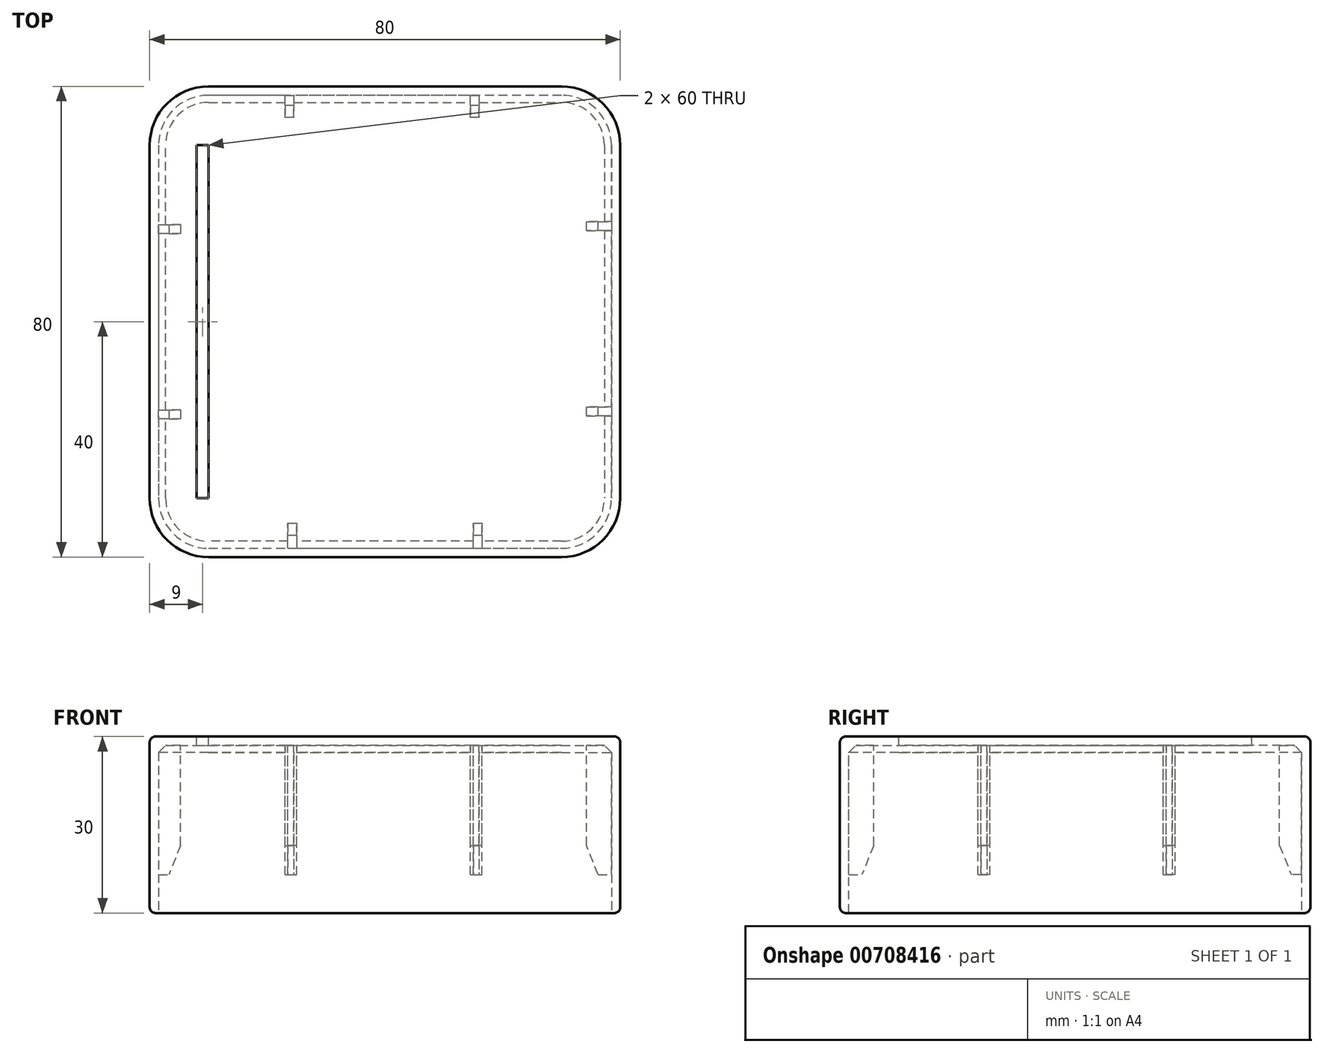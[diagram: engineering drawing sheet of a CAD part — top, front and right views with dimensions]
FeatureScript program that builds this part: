
annotation { "Feature Type Name" : "Feature", "Feature Type Description" : "" }
export const myFeature = defineFeature(function(context is Context, id is Id, definition is map)
    precondition{}
    {
        {
            var Q0;
            Q0=qCreatedBy(makeId("Top.planeOp"),FACE);
            var sketch = newSketch(context, id + "F0", { "sketchPlane" : qUnion([Q0])});
            skLineSegment(sketch, "E0", {"start": v(10, 20) * mm, "end": v(-50, 20) * mm});
            skLineSegment(sketch, "E1", {"start": v(-60, 10) * mm, "end": v(-60, -50) * mm});
            skPoint(sketch, "E2.visualSharp", {"position": v(-60, -60) * mm});
            skPoint(sketch, "E3.visualSharp", {"position": v(20, 20) * mm});
            skArc(sketch, "E3.filletArc", {"start": v(20, 10) * mm, "mid": v(17.07, 17.07) * mm, "end": v(10, 20) * mm});
            skPoint(sketch, "E4.visualSharp", {"position": v(-60, 20) * mm});
            skArc(sketch, "E4.filletArc", {"start": v(-50, 20) * mm, "mid": v(-57.07, 17.07) * mm, "end": v(-60, 10) * mm});
            skPoint(sketch, "E5.visualSharp", {"position": v(20, -60) * mm});
            skArc(sketch, "E6.filletArc", {"start": v(-60, -50) * mm, "mid": v(-57.07, -57.07) * mm, "end": v(-50, -60) * mm});
            skLineSegment(sketch, "E7", {"start": v(-50, -60) * mm, "end": v(10, -60) * mm});
            skLineSegment(sketch, "E8", {"start": v(20, 10) * mm, "end": v(20, -50) * mm});
            skArc(sketch, "E9.filletArc", {"start": v(10, -60) * mm, "mid": v(17.07, -57.07) * mm, "end": v(20, -50) * mm});
            skLineSegment(sketch, "E10", {"start": v(20, 20) * mm, "end": v(10, 20) * mm, "construction": true});
            skLineSegment(sketch, "E11", {"start": v(20, 20) * mm, "end": v(20, 10) * mm, "construction": true});
            skLineSegment(sketch, "E12", {"start": v(-50, 20) * mm, "end": v(-60, 20) * mm, "construction": true});
            skLineSegment(sketch, "E13", {"start": v(-60, 20) * mm, "end": v(-60, 10) * mm, "construction": true});
            skLineSegment(sketch, "E14", {"start": v(-60, -50) * mm, "end": v(-60, -60) * mm, "construction": true});
            skLineSegment(sketch, "E15", {"start": v(-60, -60) * mm, "end": v(-50, -60) * mm, "construction": true});
            skLineSegment(sketch, "E16", {"start": v(20, -50) * mm, "end": v(20, -60) * mm, "construction": true});
            skLineSegment(sketch, "E17", {"start": v(20, -60) * mm, "end": v(10, -60) * mm, "construction": true});
            skSolve(sketch);
        }
        {
            var Q0;
            Q0=makeQuery(id+"F0.imprint","IMPRINT",FACE,{"disambiguationData":[TD([[makeQuery(id+"F0.imprint","IMPRINT",EDGE,{"derivedFrom":sQuery(id+"F0.wireOp",EDGE,"E0")}),1.0]])]});
            extrude(context, id + "F1", {"entities" : qUnion([Q0]), "depth" : 30 * mm});
        }
        {
            var Q0;
            Q0=makeQuery(id+"F1.opExtrude","CAP_FACE",FACE,{"disambiguationData":[OSD([sQuery(id+"F0.wireOp",EDGE,"E0"),sQuery(id+"F0.wireOp",EDGE,"E1"),sQuery(id+"F0.wireOp",EDGE,"tLIrDgZX-HZ4B-HLsu-Evyy-lOQtlpBdo2Ac"),sQuery(id+"F0.wireOp",EDGE,"E3.filletArc"),sQuery(id+"F0.wireOp",EDGE,"E4.filletArc"),sQuery(id+"F0.wireOp",EDGE,"E5.filletArc"),sQuery(id+"F0.wireOp",EDGE,"yPNshCSU-yKMU-eblL-DxmT-mCKaPt0DpMVh"),sQuery(id+"F0.wireOp",EDGE,"E6.filletArc")])],"isStart":true});
            shell(context, id + "F2", {"entities" : qUnion([Q0]), "thickness" : 1.5 * mm});
        }
        {
            var Q0;
            Q0=makeQuery(id+"F2.opShell","OFFSET_FACE",FACE,{"disambiguationData":[OSD([sQuery(id+"F0.wireOp",EDGE,"E0"),sQuery(id+"F0.wireOp",EDGE,"E1"),sQuery(id+"F0.wireOp",EDGE,"E3.filletArc"),sQuery(id+"F0.wireOp",EDGE,"E4.filletArc"),sQuery(id+"F0.wireOp",EDGE,"E6.filletArc"),sQuery(id+"F0.wireOp",EDGE,"E7"),sQuery(id+"F0.wireOp",EDGE,"E8"),sQuery(id+"F0.wireOp",EDGE,"E9.filletArc")])]});
            var sketch = newSketch(context, id + "F3", { "sketchPlane" : qUnion([Q0])});
            skLineSegment(sketch, "E18", {"start": v(-36.5, 58.5) * mm, "end": v(-36.5, 54.25) * mm});
            skLineSegment(sketch, "E19", {"start": v(-36.5, 54.25) * mm, "end": v(-35, 54.25) * mm});
            skLineSegment(sketch, "E20", {"start": v(-35, 54.25) * mm, "end": v(-35, 58.5) * mm});
            skLineSegment(sketch, "E21", {"start": v(-35, 58.5) * mm, "end": v(-36.5, 58.5) * mm});
            skLineSegment(sketch, "E22", {"start": v(-5, 58.5) * mm, "end": v(-5, 54.25) * mm});
            skLineSegment(sketch, "E23", {"start": v(-5, 54.25) * mm, "end": v(-3.5, 54.25) * mm});
            skLineSegment(sketch, "E24", {"start": v(-3.5, 54.25) * mm, "end": v(-3.5, 58.5) * mm});
            skLineSegment(sketch, "E25", {"start": v(-3.5, 58.5) * mm, "end": v(-5, 58.5) * mm});
            skPoint(sketch, "E26", {"position": v(-20.25, 19.75) * mm});
            skLineSegment(sketch, "E27.1.0", {"start": v(-54.75, 3.5) * mm, "end": v(-54.75, 5) * mm});
            skLineSegment(sketch, "E27.1.1", {"start": v(-59, 36.5) * mm, "end": v(-59, 35) * mm});
            skLineSegment(sketch, "E27.1.2", {"start": v(-54.75, 35) * mm, "end": v(-54.75, 36.5) * mm});
            skLineSegment(sketch, "E27.1.3", {"start": v(-54.75, 5) * mm, "end": v(-59, 5) * mm});
            skLineSegment(sketch, "E27.1.4", {"start": v(-59, 3.5) * mm, "end": v(-54.75, 3.5) * mm});
            skLineSegment(sketch, "E27.1.5", {"start": v(-59, 5) * mm, "end": v(-59, 3.5) * mm});
            skLineSegment(sketch, "E27.1.6", {"start": v(-54.75, 36.5) * mm, "end": v(-59, 36.5) * mm});
            skLineSegment(sketch, "E27.1.7", {"start": v(-59, 35) * mm, "end": v(-54.75, 35) * mm});
            skLineSegment(sketch, "E27.2.0", {"start": v(-4, -14.75) * mm, "end": v(-5.5, -14.75) * mm});
            skLineSegment(sketch, "E27.2.1", {"start": v(-37, -19) * mm, "end": v(-35.5, -19) * mm});
            skLineSegment(sketch, "E27.2.2", {"start": v(-35.5, -14.75) * mm, "end": v(-37, -14.75) * mm});
            skLineSegment(sketch, "E27.2.3", {"start": v(-5.5, -14.75) * mm, "end": v(-5.5, -19) * mm});
            skLineSegment(sketch, "E27.2.4", {"start": v(-4, -19) * mm, "end": v(-4, -14.75) * mm});
            skLineSegment(sketch, "E27.2.5", {"start": v(-5.5, -19) * mm, "end": v(-4, -19) * mm});
            skLineSegment(sketch, "E27.2.6", {"start": v(-37, -14.75) * mm, "end": v(-37, -19) * mm});
            skLineSegment(sketch, "E27.2.7", {"start": v(-35.5, -19) * mm, "end": v(-35.5, -14.75) * mm});
            skLineSegment(sketch, "E27.3.0", {"start": v(14.25, 36) * mm, "end": v(14.25, 34.5) * mm});
            skLineSegment(sketch, "E27.3.1", {"start": v(18.5, 3) * mm, "end": v(18.5, 4.5) * mm});
            skLineSegment(sketch, "E27.3.2", {"start": v(14.25, 4.5) * mm, "end": v(14.25, 3) * mm});
            skLineSegment(sketch, "E27.3.3", {"start": v(14.25, 34.5) * mm, "end": v(18.5, 34.5) * mm});
            skLineSegment(sketch, "E27.3.4", {"start": v(18.5, 36) * mm, "end": v(14.25, 36) * mm});
            skLineSegment(sketch, "E27.3.5", {"start": v(18.5, 34.5) * mm, "end": v(18.5, 36) * mm});
            skLineSegment(sketch, "E27.3.6", {"start": v(14.25, 3) * mm, "end": v(18.5, 3) * mm});
            skLineSegment(sketch, "E27.3.7", {"start": v(18.5, 4.5) * mm, "end": v(14.25, 4.5) * mm});
            skSolve(sketch);
        }
        {
            var Q0;
            Q0=qSketchRegion(id+"F3",true);
            extrude(context, id + "F4", {"entities" : qUnion([Q0]), "operationType" : NewBodyOperationType.ADD, "depth" : 22 * mm, "offsetDistance" : 25 * mm});
        }
        {
            var Q0;
            {var subQ0=sQuery(id+"F0.wireOp",EDGE,"E0");var subQ1=sQuery(id+"F0.wireOp",EDGE,"E3.filletArc");Q0=makeQuery(id+"F4.boolean.opBoolean","SPLIT",EDGE,{"disambiguationData":[TD([makeQuery(id+"F2.opShell","OFFSET_FACE",FACE,{"disambiguationData":[OSD([subQ1])]})])],"derivedFrom":makeQuery(id+"F2.opShell","OFFSET_EDGE",EDGE,{"disambiguationData":[OSD([subQ0]),TDD([makeQuery(id+"F1.opExtrude","CAP_EDGE",EDGE,{"disambiguationData":[OSD([subQ0])],"isStart":false})])]})});}
            var Q1;
            {var subQ0=sQuery(id+"F0.wireOp",EDGE,"E0");Q1=makeQuery(id+"F4.boolean.opBoolean","SPLIT",EDGE,{"disambiguationData":[TD([makeQuery(id+"F4.opExtrude","SWEPT_FACE",FACE,{"disambiguationData":[OSD([sQuery(id+"F3.wireOp",EDGE,"E27.2.3")])]})])],"derivedFrom":makeQuery(id+"F2.opShell","OFFSET_EDGE",EDGE,{"disambiguationData":[OSD([subQ0]),TDD([makeQuery(id+"F1.opExtrude","CAP_EDGE",EDGE,{"disambiguationData":[OSD([subQ0])],"isStart":false})])]})});}
            var Q2;
            {var subQ0=sQuery(id+"F0.wireOp",EDGE,"E0");var subQ1=sQuery(id+"F0.wireOp",EDGE,"E4.filletArc");Q2=makeQuery(id+"F4.boolean.opBoolean","SPLIT",EDGE,{"disambiguationData":[TD([makeQuery(id+"F2.opShell","OFFSET_FACE",FACE,{"disambiguationData":[OSD([subQ1])]})])],"derivedFrom":makeQuery(id+"F2.opShell","OFFSET_EDGE",EDGE,{"disambiguationData":[OSD([subQ0]),TDD([makeQuery(id+"F1.opExtrude","CAP_EDGE",EDGE,{"disambiguationData":[OSD([subQ0])],"isStart":false})])]})});}
            var Q3;
            {var subQ0=sQuery(id+"F0.wireOp",EDGE,"E8");Q3=makeQuery(id+"F4.boolean.opBoolean","SPLIT",EDGE,{"disambiguationData":[TD([makeQuery(id+"F4.opExtrude","SWEPT_FACE",FACE,{"disambiguationData":[OSD([sQuery(id+"F3.wireOp",EDGE,"E27.3.3")])]})])],"derivedFrom":makeQuery(id+"F2.opShell","OFFSET_EDGE",EDGE,{"disambiguationData":[OSD([subQ0]),TDD([makeQuery(id+"F1.opExtrude","CAP_EDGE",EDGE,{"disambiguationData":[OSD([subQ0])],"isStart":false})])]})});}
            var Q4;
            {var subQ0=sQuery(id+"F0.wireOp",EDGE,"E9.filletArc");var subQ1=sQuery(id+"F0.wireOp",EDGE,"E8");Q4=makeQuery(id+"F4.boolean.opBoolean","SPLIT",EDGE,{"disambiguationData":[TD([makeQuery(id+"F2.opShell","OFFSET_FACE",FACE,{"disambiguationData":[OSD([subQ0])]})])],"derivedFrom":makeQuery(id+"F2.opShell","OFFSET_EDGE",EDGE,{"disambiguationData":[OSD([subQ1]),TDD([makeQuery(id+"F1.opExtrude","CAP_EDGE",EDGE,{"disambiguationData":[OSD([subQ1])],"isStart":false})])]})});}
            var Q5;
            {var subQ0=sQuery(id+"F0.wireOp",EDGE,"E1");Q5=makeQuery(id+"F4.boolean.opBoolean","SPLIT",EDGE,{"disambiguationData":[TD([makeQuery(id+"F4.opExtrude","SWEPT_FACE",FACE,{"disambiguationData":[OSD([sQuery(id+"F3.wireOp",EDGE,"E27.1.3")])]})])],"derivedFrom":makeQuery(id+"F2.opShell","OFFSET_EDGE",EDGE,{"disambiguationData":[OSD([subQ0]),TDD([makeQuery(id+"F1.opExtrude","CAP_EDGE",EDGE,{"disambiguationData":[OSD([subQ0])],"isStart":false})])]})});}
            var Q6;
            {var subQ0=sQuery(id+"F0.wireOp",EDGE,"E6.filletArc");var subQ1=sQuery(id+"F0.wireOp",EDGE,"E1");Q6=makeQuery(id+"F4.boolean.opBoolean","SPLIT",EDGE,{"disambiguationData":[TD([makeQuery(id+"F2.opShell","OFFSET_FACE",FACE,{"disambiguationData":[OSD([subQ0])]})])],"derivedFrom":makeQuery(id+"F2.opShell","OFFSET_EDGE",EDGE,{"disambiguationData":[OSD([subQ1]),TDD([makeQuery(id+"F1.opExtrude","CAP_EDGE",EDGE,{"disambiguationData":[OSD([subQ1])],"isStart":false})])]})});}
            var Q7;
            {var subQ0=sQuery(id+"F0.wireOp",EDGE,"E7");Q7=makeQuery(id+"F4.boolean.opBoolean","SPLIT",EDGE,{"disambiguationData":[TD([makeQuery(id+"F4.opExtrude","SWEPT_FACE",FACE,{"disambiguationData":[OSD([sQuery(id+"F3.wireOp",EDGE,"E20")])]})])],"derivedFrom":makeQuery(id+"F2.opShell","OFFSET_EDGE",EDGE,{"disambiguationData":[OSD([subQ0]),TDD([makeQuery(id+"F1.opExtrude","CAP_EDGE",EDGE,{"disambiguationData":[OSD([subQ0])],"isStart":false})])]})});}
            chamfer(context, id + "F5", {"entities" : qUnion([Q0, Q1, Q2, Q3, Q4, Q5, Q6, Q7]), "width" : 1.2 * mm, "tangentPropagation" : true});
        }
        {
            var Q0;
            Q0=makeQuery(id+"F1.opExtrude","CAP_EDGE",EDGE,{"disambiguationData":[OSD([sQuery(id+"F0.wireOp",EDGE,"E8")])],"isStart":false});
            var Q1;
            Q1=makeQuery(id+"F1.opExtrude","CAP_EDGE",EDGE,{"disambiguationData":[OSD([sQuery(id+"F0.wireOp",EDGE,"E8")])],"isStart":true});
            fillet(context, id + "F6", {"entities" : qUnion([Q0, Q1]), "radius" : 1 * mm, "tangentPropagation" : true, "allowEdgeOverflow" : false});
        }
        {
            var Q0;
            Q0=makeQuery(id+"F1.opExtrude","CAP_FACE",FACE,{"disambiguationData":[OSD([sQuery(id+"F0.wireOp",EDGE,"E0"),sQuery(id+"F0.wireOp",EDGE,"E1"),sQuery(id+"F0.wireOp",EDGE,"E3.filletArc"),sQuery(id+"F0.wireOp",EDGE,"E4.filletArc"),sQuery(id+"F0.wireOp",EDGE,"E6.filletArc"),sQuery(id+"F0.wireOp",EDGE,"E7"),sQuery(id+"F0.wireOp",EDGE,"E8"),sQuery(id+"F0.wireOp",EDGE,"E9.filletArc")])],"isStart":false});
            var sketch = newSketch(context, id + "F7", { "sketchPlane" : qUnion([Q0])});
            skLineSegment(sketch, "E28.bottom", {"start": v(-52, -50) * mm, "end": v(-50, -50) * mm});
            skLineSegment(sketch, "E28.top", {"start": v(-52, 10) * mm, "end": v(-50, 10) * mm});
            skLineSegment(sketch, "E28.left", {"start": v(-52, -50) * mm, "end": v(-52, 10) * mm});
            skLineSegment(sketch, "E28.right", {"start": v(-50, -50) * mm, "end": v(-50, 10) * mm});
            skSolve(sketch);
        }
        {
            var Q0;
            Q0=makeQuery(id+"F7.imprint","IMPRINT",FACE,{"disambiguationData":[TD([[makeQuery(id+"F7.imprint","IMPRINT",EDGE,{"derivedFrom":sQuery(id+"F7.wireOp",EDGE,"E28.bottom")}),1.0]])]});
            extrude(context, id + "F8", {"entities" : qUnion([Q0]), "operationType" : NewBodyOperationType.REMOVE, "endBound" : BoundingType.THROUGH_ALL, "oppositeDirection" : true, "depth" : 10.5 * mm, "offsetDistance" : 25 * mm});
        }
        {
            var Q0;
            Q0=makeQuery(id+"F1.opExtrude","SWEPT_FACE",FACE,{"disambiguationData":[OSD([sQuery(id+"F0.wireOp",EDGE,"E1")])]});
            cPlane(context, id + "F9", {"entities" : qUnion([Q0]), "cplaneType" : CPlaneType.OFFSET, "offset" : 40 * mm, "oppositeDirection" : true, "width" : 150 * mm, "height" : 150 * mm});
        }
        {
            var Q0;
            Q0=makeQuery(id+"F4.opExtrude","CAP_EDGE",EDGE,{"disambiguationData":[OSD([sQuery(id+"F3.wireOp",EDGE,"E27.1.0")])],"isStart":false});
            var Q1;
            Q1=makeQuery(id+"F4.opExtrude","CAP_EDGE",EDGE,{"disambiguationData":[OSD([sQuery(id+"F3.wireOp",EDGE,"E27.1.2")])],"isStart":false});
            var Q2;
            Q2=makeQuery(id+"F4.opExtrude","CAP_EDGE",EDGE,{"disambiguationData":[OSD([sQuery(id+"F3.wireOp",EDGE,"E19")])],"isStart":false});
            var Q3;
            Q3=makeQuery(id+"F4.opExtrude","CAP_EDGE",EDGE,{"disambiguationData":[OSD([sQuery(id+"F3.wireOp",EDGE,"E23")])],"isStart":false});
            var Q4;
            Q4=makeQuery(id+"F4.opExtrude","CAP_EDGE",EDGE,{"disambiguationData":[OSD([sQuery(id+"F3.wireOp",EDGE,"E27.3.0")])],"isStart":false});
            var Q5;
            Q5=makeQuery(id+"F4.opExtrude","CAP_EDGE",EDGE,{"disambiguationData":[OSD([sQuery(id+"F3.wireOp",EDGE,"E27.3.2")])],"isStart":false});
            var Q6;
            Q6=makeQuery(id+"F4.opExtrude","CAP_EDGE",EDGE,{"disambiguationData":[OSD([sQuery(id+"F3.wireOp",EDGE,"E27.2.0")])],"isStart":false});
            var Q7;
            Q7=makeQuery(id+"F4.opExtrude","CAP_EDGE",EDGE,{"disambiguationData":[OSD([sQuery(id+"F3.wireOp",EDGE,"E27.2.2")])],"isStart":false});
            chamfer(context, id + "F10", {"entities" : qUnion([Q0, Q1, Q2, Q3, Q4, Q5, Q6, Q7]), "chamferType" : ChamferType.TWO_OFFSETS, "width1" : 5 * mm, "oppositeDirection" : true, "width2" : 2 * mm, "tangentPropagation" : true});
        }
    });
